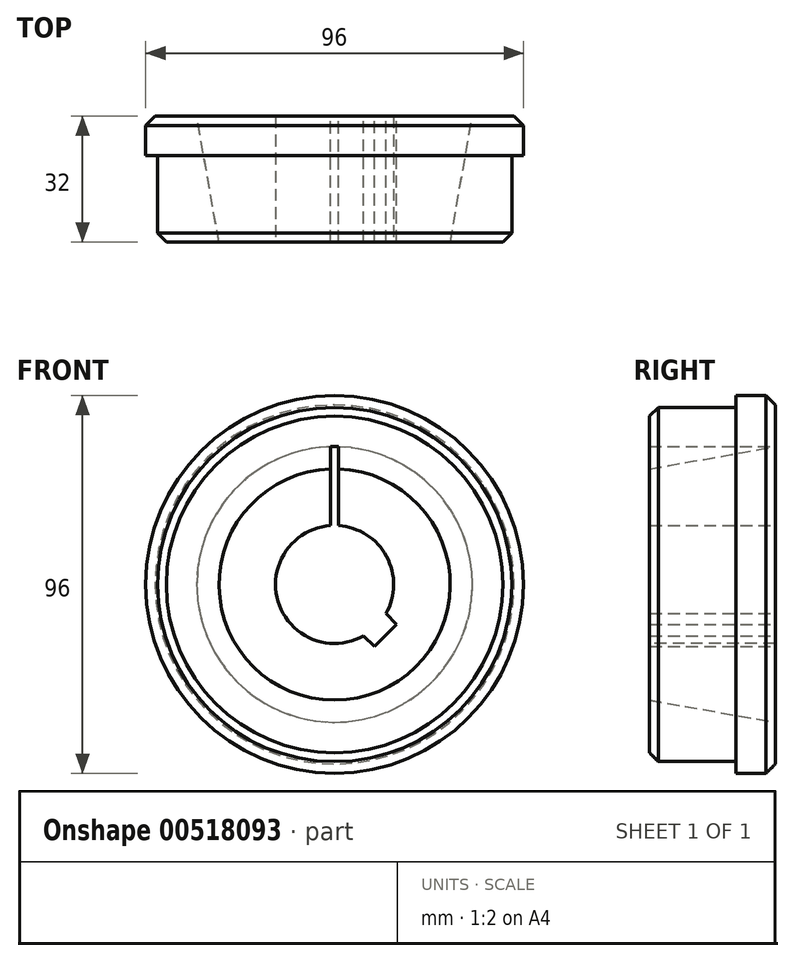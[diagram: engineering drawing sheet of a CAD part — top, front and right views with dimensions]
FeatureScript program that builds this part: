
annotation { "Feature Type Name" : "Feature", "Feature Type Description" : "" }
export const myFeature = defineFeature(function(context is Context, id is Id, definition is map)
    precondition{}
    {
        {
            var Q0;
            Q0=qCreatedBy(makeId("Right.planeOp"),FACE);
            var sketch = newSketch(context, id + "F0", { "sketchPlane" : qUnion([Q0])});
            skLineSegment(sketch, "E0", {"start": v(0, 45.6) * mm, "end": v(-2.4, 48) * mm});
            skLineSegment(sketch, "E1", {"start": v(-2.4, 48) * mm, "end": v(-10, 48) * mm});
            skLineSegment(sketch, "E2", {"start": v(-10, 48) * mm, "end": v(-10, 45) * mm});
            skLineSegment(sketch, "E3", {"start": v(-29.75, 45) * mm, "end": v(-32, 42.75) * mm});
            skLineSegment(sketch, "E4", {"start": v(-32, 42.75) * mm, "end": v(-32, 29.38) * mm});
            skLineSegment(sketch, "E5", {"start": v(-32, 0) * mm, "end": v(0, 0) * mm, "construction": true});
            skLineSegment(sketch, "E6", {"start": v(-10, 45) * mm, "end": v(-22, 45) * mm});
            skLineSegment(sketch, "E7", {"start": v(-22, 45) * mm, "end": v(-22, 45) * mm});
            skLineSegment(sketch, "E8", {"start": v(-22, 45) * mm, "end": v(-29.75, 45) * mm});
            skLineSegment(sketch, "E9", {"start": v(-2.4, 48) * mm, "end": v(0, 48) * mm, "construction": true});
            skLineSegment(sketch, "E10", {"start": v(0, 48) * mm, "end": v(0, 45.6) * mm, "construction": true});
            skLineSegment(sketch, "E11", {"start": v(-32, 42.75) * mm, "end": v(-32, 45) * mm, "construction": true});
            skLineSegment(sketch, "E12", {"start": v(-32, 45) * mm, "end": v(-29.75, 45) * mm, "construction": true});
            skLineSegment(sketch, "E13", {"start": v(0, 35.02) * mm, "end": v(0, 45.6) * mm});
            skLineSegment(sketch, "E14", {"start": v(-32, 29.38) * mm, "end": v(0, 35.02) * mm});
            skLineSegment(sketch, "E15", {"start": v(-0.1, 15) * mm, "end": v(-0.1, 35) * mm});
            skLineSegment(sketch, "E16", {"start": v(-0.1, 35) * mm, "end": v(-31.9, 29.4) * mm});
            skLineSegment(sketch, "E17", {"start": v(-31.9, 29.4) * mm, "end": v(-31.9, 15) * mm});
            skLineSegment(sketch, "E18", {"start": v(-31.9, 15) * mm, "end": v(-0.1, 15) * mm});
            skSolve(sketch);
        }
        {
            var Q0;
            Q0=makeQuery(id+"F0.imprint","IMPRINT",FACE,{"disambiguationData":[TD([[makeQuery(id+"F0.imprint","IMPRINT",EDGE,{"derivedFrom":sQuery(id+"F0.wireOp",EDGE,"E0")}),1.0]])]});
            var Q1;
            Q1=sQuery(id+"F0.wireOp",EDGE,"E5");
            revolve(context, id + "F1", {"entities" : qUnion([Q0]), "axis" : qUnion([Q1]), "revolveType" : RevolveType.FULL});
        }
        {
            var Q0;
            Q0=makeQuery(id+"F0.imprint","IMPRINT",FACE,{"disambiguationData":[TD([[makeQuery(id+"F0.imprint","IMPRINT",EDGE,{"derivedFrom":sQuery(id+"F0.wireOp",EDGE,"E15")}),1.0]])]});
            var Q1;
            Q1=sQuery(id+"F0.wireOp",EDGE,"E5");
            revolve(context, id + "F2", {"entities" : qUnion([Q0]), "axis" : qUnion([Q1]), "revolveType" : RevolveType.FULL});
        }
        {
            var Q0;
            Q0=makeQuery(id+"F2.opRevolve","SWEPT_FACE",FACE,{"disambiguationData":[OSD([sQuery(id+"F0.wireOp",EDGE,"E15")])]});
            var sketch = newSketch(context, id + "F3", { "sketchPlane" : qUnion([Q0])});
            skLineSegment(sketch, "E19", {"start": v(-1, 35.02) * mm, "end": v(1, 35.02) * mm});
            skLineSegment(sketch, "E20", {"start": v(1, 35.02) * mm, "end": v(1, 14.97) * mm});
            skLineSegment(sketch, "E21", {"start": v(-1, 35.02) * mm, "end": v(-1, 14.97) * mm});
            skArc(sketch, "E22", {"start": v(-1, 14.97) * mm, "mid": v(-13.2, 7.12) * mm, "end": v(-13.05, -7.4) * mm});
            skLineSegment(sketch, "E23", {"start": v(-13.05, -7.4) * mm, "end": v(-15.77, -10.11) * mm});
            skLineSegment(sketch, "E24", {"start": v(-15.77, -10.11) * mm, "end": v(-10.11, -15.77) * mm});
            skLineSegment(sketch, "E25", {"start": v(-10.11, -15.77) * mm, "end": v(-7.4, -13.05) * mm});
            skArc(sketch, "E26", {"start": v(1, 14.97) * mm, "mid": v(14.37, -4.3) * mm, "end": v(-7.4, -13.05) * mm});
            skLineSegment(sketch, "E27", {"start": v(0, 0) * mm, "end": v(-12.94, -12.94) * mm, "construction": true});
            skSolve(sketch);
        }
        {
            var Q0;
            Q0 = qSketchRegion(id + "F3", true);
            extrude(context, id + "F4", {"entities" : qUnion([Q0]), "operationType" : NewBodyOperationType.REMOVE, "endBound" : BoundingType.THROUGH_ALL, "oppositeDirection" : true, "depth" : 25 * mm, "offsetDistance" : 25 * mm});
        }
    });
